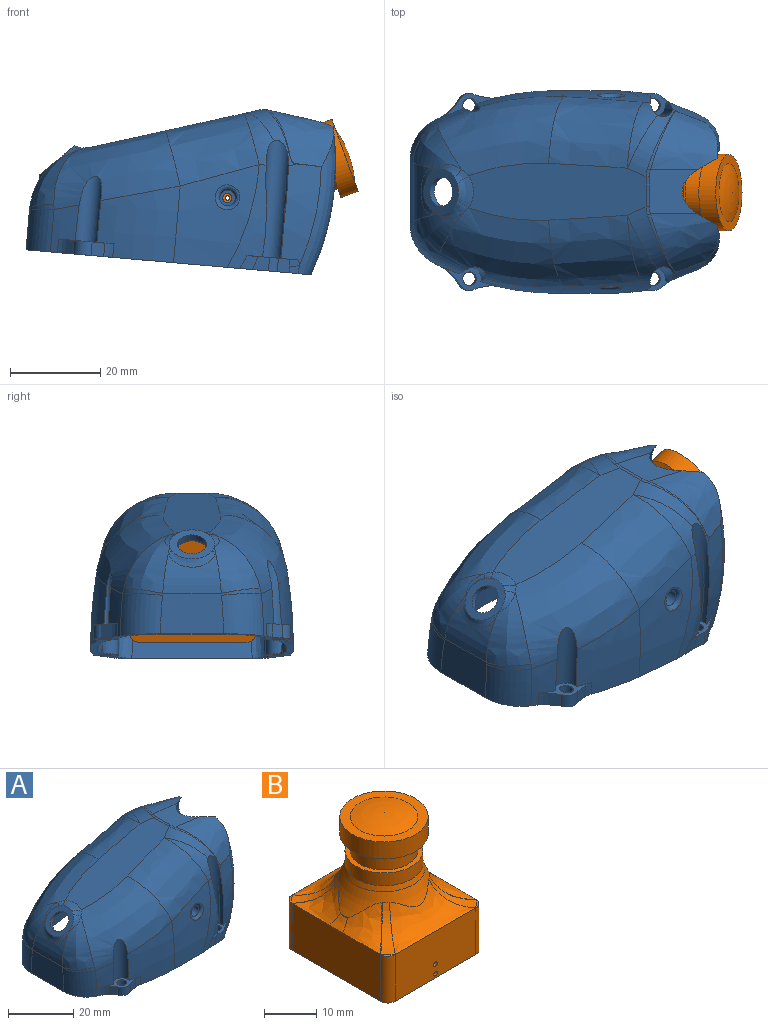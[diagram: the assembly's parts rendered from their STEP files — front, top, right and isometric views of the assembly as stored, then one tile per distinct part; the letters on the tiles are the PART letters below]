
ASSEMBLY  parts=2 mates=1
PART A: 204 faces, bbox 73x48x48.8 mm
  f0: cylinder r=1mm len=2mm, axis (0,-1,0), area 9.4mm2, adj f106,f167
  f1: plane 12.37x5.27mm, normal (0,0,1), area 18.9mm2, adj f17,f18,f142,f143,f161,f178,f179,f184
  f2: bspline ~28.37x10.63mm, area 67.9mm2, adj f3,f6,f42,f44,f71,f109,f154,f155
  f3: offset ~19.87x17.74mm, area 1mm2, adj f2,f44,f163
  f4: offset ~35.1x22.52mm, area 149.7mm2, adj f5,f44,f83,f85,f163,f170
  f5: bspline ~18.4x16.74mm, area 59.5mm2, adj f4,f6,f70,f86,f87,f163
  f6: sphere r=13.5mm, area 44mm2, adj f2,f5,f75,f163
  f7: offset ~35.1x22.52mm, area 150.3mm2, adj f9,f44,f84,f91,f162,f173
  f8: offset ~19.87x17.74mm, area 1mm2, adj f11,f44,f162
  f9: bspline ~16.43x15.82mm, area 59.9mm2, adj f7,f10,f70,f89,f90,f162
  f10: sphere r=13.5mm, area 44.5mm2, adj f9,f11,f76,f162
  f11: bspline ~27.55x10.2mm, area 68.5mm2, adj f8,f10,f41,f43,f44,f116,f148,f149
  f12: bspline ~16.87x14.74mm, area 0mm2, adj f14,f150,f159
  f13: bspline ~27.14x17.69mm, area 150.3mm2, adj f23,f59,f61,f150,f159,f190
  f14: bspline ~29x11.18mm, area 81.2mm2, adj f12,f24,f44,f48,f150,f159,f186
  f15: bspline ~27.14x17.69mm, area 150.3mm2, adj f20,f60,f67,f144,f160,f189
  f16: bspline ~16.87x14.74mm, area 0mm2, adj f22,f144,f160
  f17: torus R=44mm, axis (-1,0,0), area 247.6mm2, adj f1,f19,f44,f49,f161,f185
  f18: torus R=44mm, axis (-1,0,0), area 47.5mm2, adj f1,f19,f44,f51,f161,f184
  f19: bspline ~39.11x22.46mm, area 489.8mm2, adj f17,f18,f35,f47,f53,f55,f122,f161
  f20: bspline ~17.41x17.18mm, area 60.6mm2, adj f15,f21,f47,f65,f66,f160
  f21: sphere r=15mm, area 49.9mm2, adj f20,f22,f53,f160
  f22: bspline ~28.19x10.76mm, area 81.2mm2, adj f16,f21,f44,f49,f144,f160,f187
  f23: bspline ~19.38x18.1mm, area 60.6mm2, adj f13,f24,f47,f62,f63,f159
  f24: sphere r=15mm, area 49.9mm2, adj f14,f23,f52,f159
  f25: torus R=44mm, axis (-1,0,0), area 258.2mm2, adj f27,f44,f48,f156,f158,f183
  f26: torus R=44mm, axis (-1,0,0), area 56.8mm2, adj f27,f44,f50,f156,f158,f182
  f27: bspline ~39.11x22.46mm, area 507.5mm2, adj f25,f26,f34,f47,f52,f54,f126,f156
  f28: torus R=44mm, axis (-1,0,0), area 228.8mm2, adj f41,f44,f78,f195
  f29: torus R=44mm, axis (-1,0,0), area 237.4mm2, adj f31,f42,f44,f192
  f30: torus R=44mm, axis (-1,0,0), area 44.9mm2, adj f31,f44,f73,f193
  f31: bspline ~37.96x21.08mm, area 444.1mm2, adj f29,f30,f37,f70,f75,f77,f194
  f32: cylinder r=3.25mm len=6.5mm, axis (-0.71,0,0.71), area 30.6mm2, adj f121,f139
  f33: cylinder r=5mm len=3.79mm, axis (-0.71,0,0.71), area 0.9mm2, adj f119,f131,f132
  f34: bspline ~17.14x12.31mm, area 109mm2, adj f27,f36,f54,f127
  f35: bspline ~17.14x12.31mm, area 109mm2, adj f19,f36,f55,f123
  f36: cylinder r=15mm len=12.98mm, axis (0,-1,0), area 86.2mm2, adj f34,f35,f45,f125
  f37: bspline ~15.43x10.96mm, area 84.4mm2, adj f31,f39,f40,f77,f119,f128
  f38: bspline ~15.43x10.96mm, area 84.3mm2, adj f39,f40,f78,f79,f119,f132
  f39: cylinder r=13.5mm len=12.98mm, axis (0,-1,0), area 80.4mm2, adj f37,f38,f68,f129,f130,f131
  f40: cylinder r=13.5mm len=7.04mm, axis (0,-1,0), area 5mm2, adj f37,f38,f70,f119,f133,f134
  f41: cylinder r=102.5mm len=19.09mm, axis (1,0,0), area 156.1mm2, adj f11,f28,f44,f76,f114,f115,f200
  f42: cylinder r=102.5mm len=19.09mm, axis (1,0,0), area 156.1mm2, adj f2,f29,f44,f75,f111,f113,f198
  f43: cylinder r=102.5mm len=10.19mm, axis (1,0,0), area 18.6mm2, adj f11,f76,f116,f118
  f44: plane 63.86x45.36mm, normal (0,0,-1), area 331.8mm2, adj f2,f3,f4,f7,f8,f11,f14,f17
  f45: plane 13.93x9mm, normal (-1,0,0), area 122.6mm2, adj f36,f44,f50,f51,f54,f55
  f46: cylinder r=59.23mm len=33.18mm, axis (0,-1,0), area 342mm2, adj f44,f56,f57,f59,f60,f92,f93,f94
  f47: plane 38.43x12.71mm, normal (-0.3,0,0.95), area 439.3mm2, adj f19,f20,f23,f27,f52,f53,f64,f124
  f48: cylinder r=104mm len=23.36mm, axis (1,0,0), area 258.5mm2, adj f14,f25,f44,f52,f174
  f49: cylinder r=104mm len=23.36mm, axis (1,0,0), area 263.1mm2, adj f17,f22,f44,f53,f175
  f50: torus R=88.47mm, axis (1,0,0), area 99.4mm2, adj f26,f44,f45,f54
  f51: torus R=88.47mm, axis (1,0,0), area 99.4mm2, adj f18,f44,f45,f55
  f52: bspline ~21.55x17.21mm, area 375.1mm2, adj f24,f27,f47,f48
  f53: bspline ~21.55x17.21mm, area 375.1mm2, adj f19,f21,f47,f49
  f54: bspline ~9.17x5.66mm, area 9.6mm2, adj f27,f34,f45,f50
  f55: bspline ~9.13x5.5mm, area 9.6mm2, adj f19,f35,f45,f51
  f56: bspline ~17x14.71mm, area 181.2mm2, adj f46,f58,f59,f61,f62,f95
  f57: bspline ~17x14.71mm, area 181.2mm2, adj f46,f58,f60,f66,f67,f95
  f58: plane 10.84x9.79mm, normal (0.13,0,0.99), area 83.4mm2, adj f56,f57,f63,f64,f65,f95
  f59: bspline ~39.15x9.1mm, area 174.2mm2, adj f13,f44,f46,f56,f61,f191
  f60: bspline ~38.79x9.08mm, area 174.2mm2, adj f15,f44,f46,f57,f67,f188
  f61: bspline ~10.76x4.16mm, area 0.2mm2, adj f13,f56,f59,f62
  f62: bspline ~13.06x11.48mm, area 6.7mm2, adj f23,f56,f61,f63
  f63: bspline ~4.35x1.42mm, area 1.3mm2, adj f23,f58,f62,f64
  f64: cylinder r=1.8mm len=6.64mm, axis (0,1,0), area 5.3mm2, adj f47,f58,f63,f65
  f65: bspline ~4.35x1.42mm, area 1.3mm2, adj f20,f58,f64,f66
  f66: bspline ~13.06x11.48mm, area 6.8mm2, adj f20,f57,f65,f67
  f67: bspline ~7.99x3.08mm, area 0.2mm2, adj f15,f57,f60,f66
  f68: plane 13.93x9mm, normal (1,0,0), area 122.6mm2, adj f39,f44,f73,f74,f77,f79
  f69: cylinder r=57.73mm len=26.72mm, axis (0,-1,0), area 311.4mm2, adj f44,f83,f84,f92,f93,f94,f95,f96
  f70: plane 38.98x12.71mm, normal (0.3,0,-0.95), area 448.4mm2, adj f5,f9,f31,f40,f75,f76,f78,f88
  f71: cylinder r=102.5mm len=10.19mm, axis (1,0,0), area 18.6mm2, adj f2,f75,f109,f110
  f72: torus R=44mm, axis (-1,0,0), area 38mm2, adj f44,f74,f78,f196
  f73: torus R=88.47mm, axis (1,0,0), area 83.8mm2, adj f30,f44,f68,f77
  f74: torus R=88.47mm, axis (1,0,0), area 83.8mm2, adj f44,f68,f72,f79
  f75: bspline ~21.1x16.03mm, area 337.2mm2, adj f6,f31,f42,f70,f71,f112
  f76: bspline ~21.1x16.03mm, area 337.2mm2, adj f10,f41,f43,f70,f78,f117
  f77: bspline ~7.82x4.81mm, area 7.6mm2, adj f31,f37,f68,f73
  f78: bspline ~37.96x21.08mm, area 432mm2, adj f28,f38,f70,f72,f76,f79,f197
  f79: bspline ~7.79x4.68mm, area 7.6mm2, adj f38,f68,f74,f78
  f80: offset ~20x17.92mm, area 125.4mm2, adj f82,f85,f86,f95,f168
  f81: offset ~20x17.92mm, area 125.3mm2, adj f82,f90,f91,f95,f172
  f82: plane 9.8x7.29mm, normal (-0.13,0,-0.99), area 48.4mm2, adj f80,f81,f87,f88,f89,f95
  f83: bspline ~26.22x6.61mm, area 89mm2, adj f4,f44,f69,f169
  f84: bspline ~26.04x6.54mm, area 89mm2, adj f7,f44,f69,f171
  f85: bspline ~10.76x4.16mm, area 0mm2, adj f4,f80,f86,f170
  f86: bspline ~12.96x10.29mm, area 1mm2, adj f5,f80,f85,f87
  f87: bspline ~3.96x0.76mm, area 0.2mm2, adj f5,f82,f86,f88
  f88: cylinder r=0.3mm len=6.64mm, axis (0,1,0), area 0.9mm2, adj f70,f82,f87,f89
  f89: bspline ~3.96x0.76mm, area 0.2mm2, adj f9,f82,f88,f90
  f90: bspline ~12.96x10.29mm, area 1mm2, adj f9,f81,f89,f91
  f91: bspline ~10.75x4.16mm, area 0mm2, adj f7,f81,f90,f173
  f92: cylinder r=9.5mm len=4.82mm, axis (0.97,0,0.26), area 6.7mm2, adj f46,f69,f93,f96
  f93: cylinder r=9.5mm len=19mm, axis (0.97,0,0.26), area 56mm2, adj f46,f69,f92,f94
  f94: cylinder r=9.5mm len=4.82mm, axis (0.97,0,0.26), area 6.7mm2, adj f46,f69,f93,f97
  f95: cylinder r=9.5mm len=19mm, axis (0.97,0,0.26), area 99.1mm2, adj f46,f56,f57,f58,f69,f80,f81,f82
  f96: cylinder r=2mm len=1.87mm, axis (0.97,0,0.26), area 1.4mm2, adj f46,f69,f92,f95
  f97: cylinder r=2mm len=1.87mm, axis (0.97,0,0.26), area 1.4mm2, adj f46,f69,f94,f95
  f98: cylinder r=1mm len=2mm, axis (0,-1,0), area 9.4mm2, adj f100,f165
  f99: plane 5.92x3.35mm, normal (-1,0,0), area 14.3mm2, adj f100,f101,f102,f114,f200,f203
  f100: plane 5.99x5mm, normal (0,1,0), area 24.1mm2, adj f98,f99,f102,f103,f203
  f101: plane 5x0.05mm, normal (0,0,-1), area 0.2mm2, adj f99,f103,f200,f203
  f102: cylinder r=2.5mm len=5mm, axis (0,1,0), area 16.2mm2, adj f99,f100,f103,f115,f117,f118
  f103: plane 5.92x3.35mm, normal (1,0,0), area 14.3mm2, adj f100,f101,f102,f116,f200,f203
  f104: plane 5x0.05mm, normal (0,0,-1), area 0.2mm2, adj f105,f107,f198,f202
  f105: plane 5.92x3.35mm, normal (1,0,0), area 14.3mm2, adj f104,f106,f108,f109,f198,f202
  f106: plane 5.99x5mm, normal (0,-1,0), area 24.1mm2, adj f0,f105,f107,f108,f202
  f107: plane 5.92x3.35mm, normal (-1,0,0), area 14.3mm2, adj f104,f106,f108,f111,f198,f202
  f108: cylinder r=2.5mm len=5mm, axis (0,-1,0), area 16.2mm2, adj f105,f106,f107,f110,f112,f113
  f109: torus R=99.5mm, axis (-1,0,0), area 33.7mm2, adj f2,f71,f105,f110,f198,f199
  f110: bspline ~6.88x5.25mm, area 23.8mm2, adj f71,f108,f109,f112
  f111: torus R=99.5mm, axis (-1,0,0), area 33.7mm2, adj f42,f107,f113,f198
  f112: bspline ~6.78x5.33mm, area 23.6mm2, adj f75,f108,f110,f113
  f113: bspline ~5.26x4.06mm, area 11.3mm2, adj f42,f108,f111,f112
  f114: torus R=99.5mm, axis (1,0,0), area 33.7mm2, adj f41,f99,f115,f200
  f115: bspline ~5.1x3.98mm, area 11.3mm2, adj f41,f102,f114,f117
  f116: torus R=99.5mm, axis (1,0,0), area 33.7mm2, adj f11,f43,f103,f118,f200,f201
  f117: bspline ~6.65x5.33mm, area 23.6mm2, adj f76,f102,f115,f118
  f118: bspline ~6.89x5.28mm, area 23.8mm2, adj f43,f102,f116,f117
  f119: plane 10.14x6.83mm, normal (0.71,0,-0.71), area 20.9mm2, adj f33,f37,f38,f40,f120,f128,f130,f132
  f120: cylinder r=5mm len=3.79mm, axis (-0.71,0,0.71), area 0.9mm2, adj f119,f128,f129
  f121: plane 10.27x7.35mm, normal (-0.71,0,0.71), area 45.4mm2, adj f32,f122,f123,f124,f125,f126,f127
  f122: bspline ~3.12x3.05mm, area 4.9mm2, adj f19,f121,f123,f124
  f123: bspline ~6.69x5.16mm, area 8.6mm2, adj f35,f121,f122,f125
  f124: bspline ~7.08x3.61mm, area 18.6mm2, adj f47,f121,f122,f126
  f125: bspline ~10.31x3.68mm, area 20.4mm2, adj f36,f121,f123,f127
  f126: bspline ~3.12x3.05mm, area 4.9mm2, adj f27,f121,f124,f127
  f127: bspline ~6.41x4.99mm, area 8.6mm2, adj f34,f121,f125,f126
  f128: bspline ~6.18x4.73mm, area 8.8mm2, adj f37,f119,f120,f129
  f129: bspline ~3.23x3.14mm, area 2.7mm2, adj f39,f120,f128,f130
  f130: bspline ~7.9x1.83mm, area 9.5mm2, adj f39,f119,f129,f131
  f131: bspline ~2.93x2.76mm, area 2.7mm2, adj f33,f39,f130,f132
  f132: bspline ~6.66x5.3mm, area 8.8mm2, adj f33,f38,f119,f131
  f133: plane 4.1x2.61mm, normal (-0.61,-0.5,-0.61), area 5.7mm2, adj f40,f119,f134,f137,f139
  f134: plane 4.1x2.61mm, normal (-0.61,0.5,-0.61), area 5.7mm2, adj f40,f119,f133,f138,f139
  f135: plane 4.1x2.52mm, normal (0.61,0.5,0.61), area 5.7mm2, adj f119,f136,f138,f139
  f136: plane 4.1x2.52mm, normal (0.61,-0.5,0.61), area 5.7mm2, adj f119,f135,f137,f139
  f137: plane 4.2x4.2mm, normal (0,-1,0), area 5.7mm2, adj f119,f133,f136,f139
  f138: plane 4.2x4.2mm, normal (0,1,0), area 5.7mm2, adj f119,f134,f135,f139
  f139: plane 8.2x6.7mm, normal (0.71,0,-0.71), area 25mm2, adj f32,f133,f134,f135,f136,f137,f138
  f140: cylinder r=2.59mm len=13.24mm, axis (0,0,-1), area 28.1mm2, adj f44,f192,f193,f194
  f141: cylinder r=2.61mm len=14.06mm, axis (0,0,-1), area 35.7mm2, adj f44,f195,f196,f197
  f142: cylinder r=2.6mm len=3.97mm, axis (0,0,-1), area 14.6mm2, adj f1,f44,f178,f179
  f143: cylinder r=1.5mm len=3mm, axis (0,0,-1), area 28.3mm2, adj f1,f44
  f144: plane 11.62x5.65mm, normal (0,0,1), area 16.7mm2, adj f15,f16,f22,f145,f146,f147,f160,f177
  f145: plane 3.69x3.01mm, normal (0.05,-1,0), area 9.3mm2, adj f44,f144,f147,f187
  f146: cylinder r=1.5mm len=3mm, axis (0,0,-1), area 28.3mm2, adj f44,f144
  f147: cylinder r=2.6mm len=3mm, axis (0,0,-1), area 6.7mm2, adj f44,f144,f145,f177
  f148: plane 0.08x0.02mm, normal (-0.58,0.81,0), area 0mm2, adj f11,f149,f162
  f149: plane 0.03x0.02mm, normal (0,0,1), area 0mm2, adj f11,f148,f162
  f150: plane 11.62x5.65mm, normal (0,0,1), area 16.7mm2, adj f12,f13,f14,f151,f152,f153,f159,f176
  f151: plane 3.69x3.01mm, normal (0.05,1,0), area 9.3mm2, adj f44,f150,f153,f186
  f152: cylinder r=1.5mm len=3mm, axis (0,0,-1), area 28.3mm2, adj f44,f150
  f153: cylinder r=2.6mm len=3mm, axis (0,0,-1), area 6.7mm2, adj f44,f150,f151,f176
  f154: plane 0.02x0.01mm, normal (-0.58,-0.81,0), area 0mm2, adj f2,f155,f163
  f155: plane 0.01x0mm, normal (0,0,1), area 0mm2, adj f2,f154,f163
  f156: cylinder r=1.5mm len=14.99mm, axis (0,0,-1), area 67.7mm2, adj f25,f26,f27,f44,f158
  f157: cylinder r=2.6mm len=3.97mm, axis (0,0,-1), area 14.6mm2, adj f44,f158,f180,f181
  f158: plane 12.38x5.28mm, normal (0,0,1), area 12.3mm2, adj f25,f26,f156,f157,f180,f181,f182,f183
  f159: cylinder r=2.6mm len=26.01mm, axis (0,0,-1), area 245.5mm2, adj f12,f13,f14,f23,f24,f150
  f160: cylinder r=2.6mm len=26.01mm, axis (0,0,-1), area 245.5mm2, adj f15,f16,f20,f21,f22,f144
  f161: cylinder r=2.6mm len=14.53mm, axis (0,0,-1), area 89.4mm2, adj f1,f17,f18,f19
  f162: cylinder r=2.71mm len=26.8mm, axis (0,0,-1), area 203.7mm2, adj f7,f8,f9,f10,f11,f44,f148,f149
  f163: cylinder r=2.73mm len=26.93mm, axis (0,0,-1), area 208.7mm2, adj f2,f3,f4,f5,f6,f44,f154,f155
  f164: cylinder r=1.75mm len=4.2mm, axis (0,1,0), area 46.2mm2, adj f165,f175
  f165: plane 3.5x3.5mm, normal (0,-1,0), area 6.5mm2, adj f98,f164
  f166: cylinder r=2mm len=5.05mm, axis (0,-1,0), area 63.5mm2, adj f167,f174
  f167: plane 4x4mm, normal (0,1,0), area 9.4mm2, adj f0,f166
  f168: bspline ~20.25x10.9mm, area 52.8mm2, adj f69,f80,f95,f169,f170
  f169: bspline ~5.72x2.43mm, area 0.1mm2, adj f83,f168,f170
  f170: bspline ~0.77x0.37mm, area 0mm2, adj f4,f85,f168,f169
  f171: bspline ~5.72x2.43mm, area 0.1mm2, adj f84,f172,f173
  f172: bspline ~20.3x10.92mm, area 52.8mm2, adj f69,f81,f95,f171,f173
  f173: bspline ~0.77x0.37mm, area 0mm2, adj f7,f91,f171,f172
  f174: bspline ~6.07x6.01mm, area 23.8mm2, adj f48,f166
  f175: bspline ~5.55x5.51mm, area 21.2mm2, adj f49,f164
  f176: bspline ~4.07x2.84mm, area 9.5mm2, adj f44,f150,f153,f190,f191
  f177: bspline ~4.07x2.84mm, area 9.5mm2, adj f44,f144,f147,f188,f189
  f178: bspline ~3.91x3.48mm, area 8.6mm2, adj f1,f44,f142,f185
  f179: bspline ~3.45x3mm, area 8.6mm2, adj f1,f44,f142,f184
  f180: bspline ~3.91x3.48mm, area 8.6mm2, adj f44,f157,f158,f183
  f181: bspline ~3.45x3mm, area 8.6mm2, adj f44,f157,f158,f182
  f182: bspline ~4.28x1.63mm, area 6.1mm2, adj f26,f44,f158,f181
  f183: bspline ~4.29x2.09mm, area 6.1mm2, adj f25,f44,f158,f180
  f184: bspline ~4.26x1.64mm, area 6.1mm2, adj f1,f18,f44,f179
  f185: bspline ~4.31x2.08mm, area 6.1mm2, adj f1,f17,f44,f178
  f186: bspline ~6.19x4.38mm, area 7.9mm2, adj f14,f44,f150,f151
  f187: bspline ~5.98x4.26mm, area 7.9mm2, adj f22,f44,f144,f145
  f188: bspline ~4.09x2.36mm, area 3.6mm2, adj f44,f60,f177,f189
  f189: bspline ~2.81x2.47mm, area 3.7mm2, adj f15,f144,f177,f188
  f190: bspline ~2.82x2.47mm, area 3.7mm2, adj f13,f150,f176,f191
  f191: bspline ~4.1x2.36mm, area 3.6mm2, adj f44,f59,f176,f190
  f192: bspline ~14.06x2.87mm, area 31.9mm2, adj f29,f44,f140,f194
  f193: bspline ~13.21x3.37mm, area 28.6mm2, adj f30,f44,f140,f194
  f194: bspline ~5.76x5.7mm, area 15.1mm2, adj f31,f140,f192,f193
  f195: bspline ~14.85x3.12mm, area 38mm2, adj f28,f44,f141,f197
  f196: bspline ~14.9x3.76mm, area 32.8mm2, adj f44,f72,f141,f197
  f197: bspline ~7.41x7.23mm, area 25.5mm2, adj f78,f141,f195,f196
  f198: plane 10.58x6.18mm, normal (0,-0.51,-0.86), area 35.5mm2, adj f42,f104,f105,f107,f109,f111,f199
  f199: bspline ~5.4x3.34mm, area 0.2mm2, adj f2,f109,f198
  f200: plane 10.58x6.18mm, normal (0,0.51,-0.86), area 35.5mm2, adj f41,f99,f101,f103,f114,f116,f201
  f201: bspline ~5.4x3.34mm, area 0.2mm2, adj f11,f116,f200
  f202: plane 5x1.15mm, normal (0,-0.71,-0.71), area 8.1mm2, adj f104,f105,f106,f107
  f203: plane 5x1.15mm, normal (0,0.71,-0.71), area 8.1mm2, adj f99,f100,f101,f103
PART B: 42 faces, bbox 32.5x35.3x32.6 mm
  f0: cone r=12.5mm half-angle=37.1deg, axis (0,0,-1), area 0mm2, adj f16,f20
  f1: plane 2.06x1.88mm, normal (0,0,1), area 1mm2, adj f9,f10,f23
  f2: plane 2.05x1.88mm, normal (0,0,1), area 1mm2, adj f8,f9,f19
  f3: plane 2.06x1.88mm, normal (0,0,1), area 1mm2, adj f5,f6,f26
  f4: cylinder r=2mm len=11mm, axis (0,0,-1), area 34.6mm2, adj f5,f11,f12,f13,f32
  f5: plane 22.7x11.7mm, normal (0,1,0), area 240.4mm2, adj f3,f4,f6,f12,f13,f28,f40,f41
  f6: cylinder r=2mm len=11mm, axis (0,0,-1), area 34.6mm2, adj f3,f5,f7,f13,f24
  f7: plane 24.67x11.67mm, normal (-1,0,0), area 264mm2, adj f6,f8,f13,f18,f20,f22
  f8: cylinder r=2mm len=11mm, axis (0,0,-1), area 34.6mm2, adj f2,f7,f9,f13,f17
  f9: plane 22.7x11.7mm, normal (0,-1,0), area 240.4mm2, adj f1,f2,f8,f10,f13,f21,f40,f41
  f10: cylinder r=2mm len=11mm, axis (0,0,-1), area 34.6mm2, adj f1,f9,f11,f13,f25
  f11: plane 24.67x11.67mm, normal (1,0,0), area 264mm2, adj f4,f10,f13,f27,f29,f31
  f12: plane 2.05x1.88mm, normal (0,0,1), area 1mm2, adj f4,f5,f30
  f13: plane 28x26mm, normal (0,0,-1), area 724.6mm2, adj f4,f5,f6,f7,f8,f9,f10,f11
  f14: cone r=7.5mm half-angle=18.4deg, axis (0,0,-1), area 58.4mm2, adj f16,f33
  f15: cone r=12.5mm half-angle=37.1deg, axis (0,0,-1), area 0mm2, adj f16,f29
  f16: torus R=26.86mm, axis (0,0,1), area 195.9mm2, adj f0,f14,f15,f17,f18,f19,f21,f22
  f17: bspline ~6.65x6.25mm, area 0.8mm2, adj f8,f16,f18,f19
  f18: bspline ~10.98x6.59mm, area 52.4mm2, adj f7,f16,f17,f20
  f19: bspline ~8.08x7.65mm, area 22.7mm2, adj f2,f16,f17,f21
  f20: bspline ~3.55x2.15mm, area 8.2mm2, adj f0,f7,f18,f22
  f21: bspline ~21.89x7.16mm, area 126mm2, adj f9,f16,f19,f23
  f22: bspline ~11.33x6.59mm, area 52.4mm2, adj f7,f16,f20,f24
  f23: bspline ~11.23x10.5mm, area 22.7mm2, adj f1,f16,f21,f25
  f24: bspline ~6.65x6.25mm, area 0.9mm2, adj f6,f16,f22,f26
  f25: bspline ~6.65x6.25mm, area 0.9mm2, adj f10,f16,f23,f27
  f26: bspline ~12.08x12.05mm, area 22.7mm2, adj f3,f16,f24,f28
  f27: bspline ~11.34x6.63mm, area 52.4mm2, adj f11,f16,f25,f29
  f28: bspline ~21.89x7.16mm, area 126mm2, adj f5,f16,f26,f30
  f29: bspline ~3.56x2.17mm, area 8.2mm2, adj f11,f15,f27,f31
  f30: bspline ~15.22x14.81mm, area 22.7mm2, adj f12,f16,f28,f32
  f31: bspline ~10.98x6.59mm, area 52.4mm2, adj f11,f16,f29,f32
  f32: bspline ~6.65x6.25mm, area 0.8mm2, adj f4,f16,f30,f31
  f33: cylinder r=7.5mm len=15mm, axis (0,0,1), area 141.4mm2, adj f14,f34
  f34: plane 15x15mm, normal (0,0,1), area 44mm2, adj f33,f35
  f35: cylinder r=6.5mm len=13mm, axis (0,0,-1), area 163.4mm2, adj f34,f38
  f36: cylinder r=8.5mm len=17mm, axis (0,0,-1), area 213.6mm2, adj f37,f38
  f37: plane 17x17mm, normal (0,0,1), area 94.2mm2, adj f36,f39
  f38: plane 17x17mm, normal (0,0,-1), area 94.2mm2, adj f35,f36
  f39: torus R=0.04mm, axis (0,0,1), area 135.1mm2, adj f37
  f40: cylinder r=0.5mm len=28mm, axis (0,-1,0), area 88mm2, adj f5,f9
  f41: cylinder r=0.5mm len=28mm, axis (0,-1,0), area 88mm2, adj f5,f9
PLACE A rot(axis=(0,1,0),5deg) t=(9.06,8.36,6.98)mm fixed
PLACE B rot(axis=(0,1,0),70deg) t=(6.16,13.23,21.24)mm
MATE revolute B.f40 <-> A.f102  axis (0,-1,0) through (9.22,-0.77,22.35)mm
